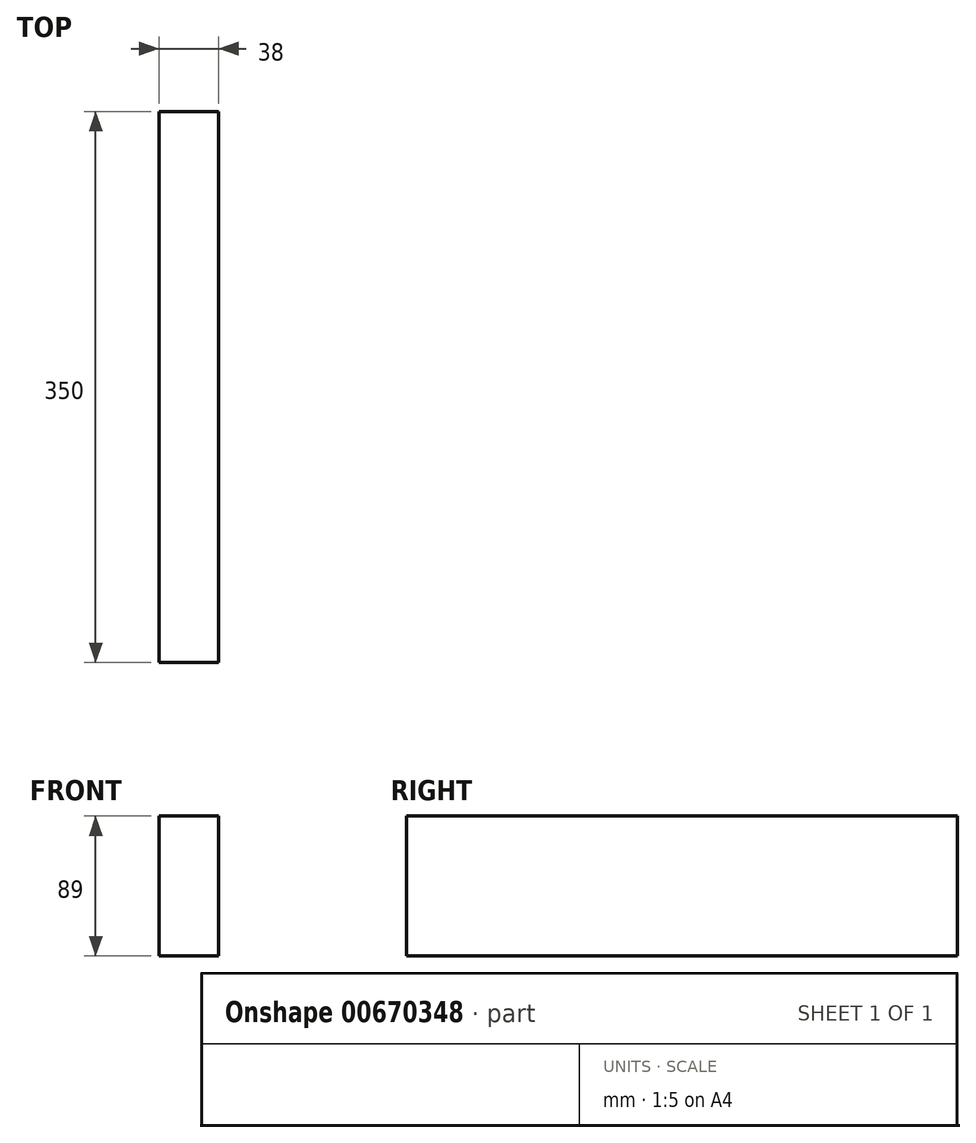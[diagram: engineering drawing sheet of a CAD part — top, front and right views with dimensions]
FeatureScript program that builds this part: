
annotation { "Feature Type Name" : "Feature", "Feature Type Description" : "" }
export const myFeature = defineFeature(function(context is Context, id is Id, definition is map)
    precondition{}
    {
        {
            var Q0;
            Q0=qCreatedBy(makeId("Front.planeOp"),FACE);
            var sketch = newSketch(context, id + "F0", { "sketchPlane" : qUnion([Q0])});
            skLineSegment(sketch, "E0.bottom", {"start": v(-19, 44.5) * mm, "end": v(19, 44.5) * mm});
            skLineSegment(sketch, "E0.top", {"start": v(-19, -44.5) * mm, "end": v(19, -44.5) * mm});
            skLineSegment(sketch, "E0.left", {"start": v(-19, 44.5) * mm, "end": v(-19, -44.5) * mm});
            skLineSegment(sketch, "E0.right", {"start": v(19, 44.5) * mm, "end": v(19, -44.5) * mm});
            skPoint(sketch, "E0.middle", {"position": v(0, 0) * mm});
            skSolve(sketch);
        }
        {
            var Q0;
            Q0 = qSketchRegion(id + "F0", true);
            extrude(context, id + "F1", {"entities" : qUnion([Q0]), "endBound" : BoundingType.SYMMETRIC, "depth" : 350 * mm, "offsetDistance" : 25 * mm});
        }
    });
